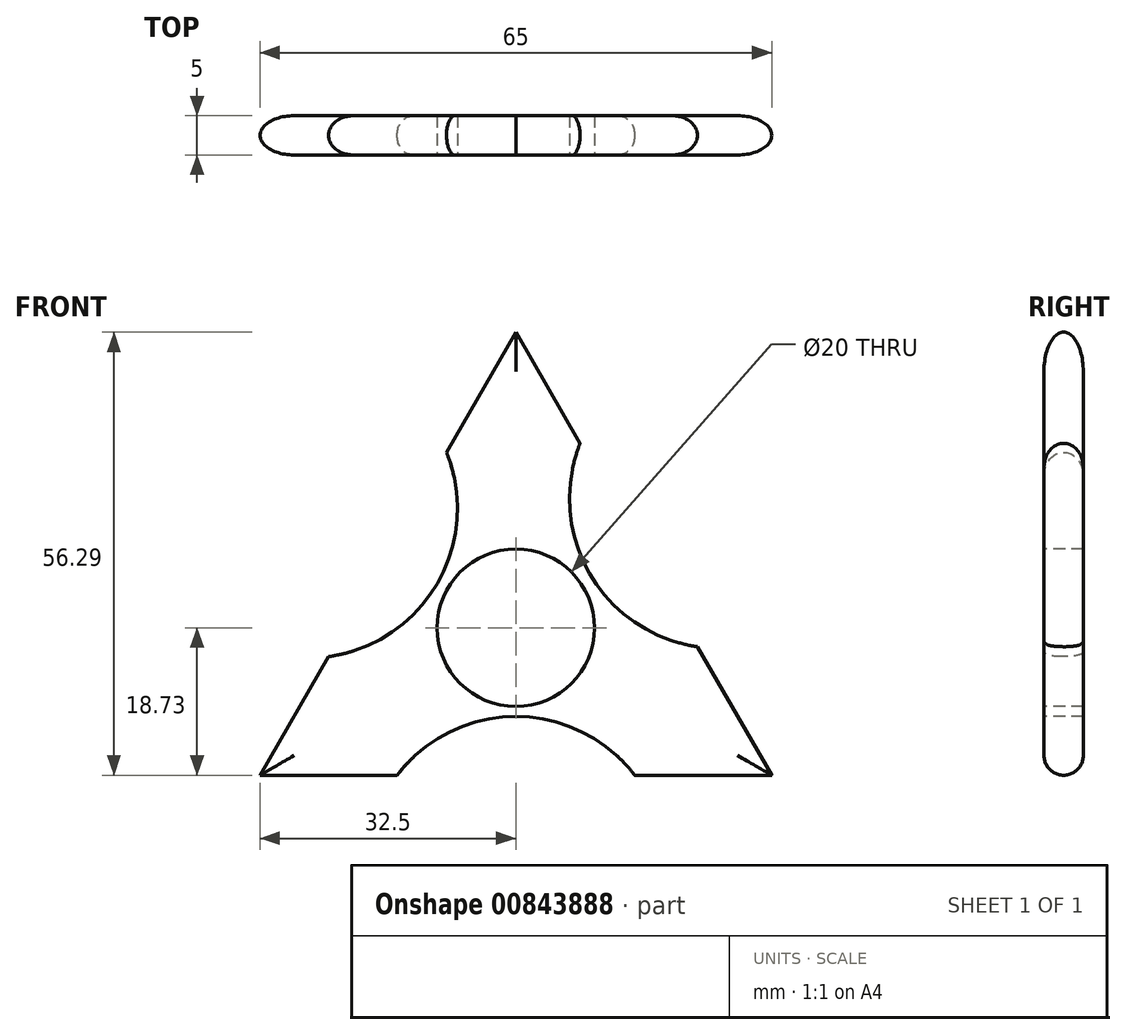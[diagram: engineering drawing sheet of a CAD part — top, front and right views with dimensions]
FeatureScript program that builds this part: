
annotation { "Feature Type Name" : "Feature", "Feature Type Description" : "" }
export const myFeature = defineFeature(function(context is Context, id is Id, definition is map)
    precondition{}
    {
        {
            var Q0;
            Q0=qCreatedBy(makeId("Front.planeOp"),FACE);
            var sketch = newSketch(context, id + "F0", { "sketchPlane" : qUnion([Q0])});
            skLineSegment(sketch, "E0", {"start": v(-32.5, 0) * mm, "end": v(32.5, 0) * mm});
            skLineSegment(sketch, "E1", {"start": v(32.5, 0) * mm, "end": v(0, 56.3) * mm});
            skLineSegment(sketch, "E2", {"start": v(0, 56.3) * mm, "end": v(-32.5, 0) * mm});
            skSolve(sketch);
        }
        {
            var Q0;
            Q0=makeQuery(id+"F0.imprint","IMPRINT",FACE,{"disambiguationData":[TD([[makeQuery(id+"F0.imprint","IMPRINT",EDGE,{"derivedFrom":sQuery(id+"F0.wireOp",EDGE,"E0")}),1.0]])]});
            var sketch = newSketch(context, id + "F1", { "sketchPlane" : qUnion([Q0])});
            skCircle(sketch, "E3", {"center": v(0, 18.73) * mm, "radius": 9.5 * mm});
            skEllipse(sketch, "E4", {"center": v(-16.73, 28.4) * mm, "majorRadius": 15 * mm, "minorRadius": 7.5 * mm, "majorAxis": v(0.52, 0.86)});
            skEllipse(sketch, "E5", {"center": v(16.42, 28.27) * mm, "majorRadius": 15 * mm, "minorRadius": 7.5 * mm, "majorAxis": v(-0.5, 0.86)});
            skEllipse(sketch, "E6", {"center": v(0, 0) * mm, "majorRadius": 15 * mm, "minorRadius": 7.5 * mm, "majorAxis": v(-1, 0)});
            skLineSegment(sketch, "E7", {"start": v(16.42, 28.27) * mm, "end": v(-32.54, 0) * mm});
            skLineSegment(sketch, "E8", {"start": v(0, 56.42) * mm, "end": v(0, 0) * mm});
            skPoint(sketch, "E9", {"position": v(32.46, 0) * mm});
            skLineSegment(sketch, "E10", {"start": v(32.46, 0) * mm, "end": v(-16.73, 28.4) * mm});
            skSolve(sketch);
        }
        {
            var Q0;
            Q0=makeQuery(id+"F0.imprint","IMPRINT",FACE,{"disambiguationData":[TD([[makeQuery(id+"F0.imprint","IMPRINT",EDGE,{"derivedFrom":sQuery(id+"F0.wireOp",EDGE,"E0")}),1.0]])]});
            extrude(context, id + "F2", {"entities" : qUnion([Q0]), "depth" : 5 * mm, "offsetDistance" : 25 * mm});
        }
        {
            var Q0;
            Q0=sQuery(id+"F1.wireOp",VERTEX,"E3.center");
            var Q1;
            Q1=makeQuery(id+"F2.opExtrude","SWEPT_BODY",BODY,{"disambiguationData":[OSD([sQuery(id+"F0.wireOp",EDGE,"E0"),sQuery(id+"F0.wireOp",EDGE,"E1"),sQuery(id+"F0.wireOp",EDGE,"E2")])]});
            hole(context, id + "F3", {"style" : HoleStyle.SIMPLE, "endStyle" : HoleEndStyle.THROUGH, "oppositeDirection" : true, "holeDiameter" : 20 * mm, "majorDiameter" : 5 * mm, "isTappedThrough" : true, "tappedDepth" : 12 * mm, "tapClearance" : 3, "startFromSketch" : true, "locations" : qUnion([Q0]), "scope" : qUnion([Q1])});
        }
        {
            var Q0;
            Q0=makeQuery(id+"F2.opExtrude","CAP_FACE",FACE,{"disambiguationData":[OSD([sQuery(id+"F0.wireOp",EDGE,"E0"),sQuery(id+"F0.wireOp",EDGE,"E1"),sQuery(id+"F0.wireOp",EDGE,"E2")])],"isStart":false});
            var sketch = newSketch(context, id + "F4", { "sketchPlane" : qUnion([Q0])});
            skArc(sketch, "E11", {"start": v(-23.8, 15.07) * mm, "mid": v(-9.97, 24.39) * mm, "end": v(-8.81, 41.02) * mm});
            skArc(sketch, "E12", {"start": v(8.16, 42.16) * mm, "mid": v(9.35, 25.63) * mm, "end": v(23.07, 16.33) * mm});
            skArc(sketch, "E13", {"start": v(15.1, 0) * mm, "mid": v(0, 7.46) * mm, "end": v(-15.1, 0) * mm});
            skSolve(sketch);
        }
        {
            var Q0;
            {var subQ0=sQuery(id+"F4.wireOp",EDGE,"E11");Q0=makeQuery(id+"F4.imprint","IMPRINT",FACE,{"disambiguationData":[TD([[makeQuery(id+"F4.imprint","IMPRINT",EDGE,{"derivedFrom":subQ0}),1.0]])]});}
            var Q1;
            {var subQ0=sQuery(id+"F4.wireOp",EDGE,"E12");Q1=makeQuery(id+"F4.imprint","IMPRINT",FACE,{"disambiguationData":[TD([[makeQuery(id+"F4.imprint","IMPRINT",EDGE,{"derivedFrom":subQ0}),1.0]])]});}
            var Q2;
            {var subQ0=sQuery(id+"F4.wireOp",EDGE,"E13");Q2=makeQuery(id+"F4.imprint","IMPRINT",FACE,{"disambiguationData":[TD([[makeQuery(id+"F4.imprint","IMPRINT",EDGE,{"derivedFrom":subQ0}),1.0]])]});}
            extrude(context, id + "F5", {"entities" : qUnion([Q0, Q1, Q2]), "operationType" : NewBodyOperationType.REMOVE, "oppositeDirection" : true, "depth" : 5 * mm, "offsetDistance" : 25 * mm});
        }
        {
            var Q0;
            {var subQ0=sQuery(id+"F0.wireOp",EDGE,"E2");var subQ1=sQuery(id+"F0.wireOp",EDGE,"E1");Q0=makeQuery(id+"F5.boolean.opBoolean","SPLIT",EDGE,{"disambiguationData":[TD([makeQuery(id+"F2.opExtrude","SWEPT_FACE",FACE,{"disambiguationData":[OSD([subQ1])]})])],"derivedFrom":makeQuery(id+"F2.opExtrude","CAP_EDGE",EDGE,{"disambiguationData":[OSD([subQ0])],"isStart":false})});}
            var Q1;
            {var subQ0=sQuery(id+"F0.wireOp",EDGE,"E2");var subQ1=sQuery(id+"F0.wireOp",EDGE,"E1");Q1=makeQuery(id+"F5.boolean.opBoolean","SPLIT",EDGE,{"disambiguationData":[TD([makeQuery(id+"F2.opExtrude","SWEPT_FACE",FACE,{"disambiguationData":[OSD([subQ0])]})])],"derivedFrom":makeQuery(id+"F2.opExtrude","CAP_EDGE",EDGE,{"disambiguationData":[OSD([subQ1])],"isStart":false})});}
            var Q2;
            {var subQ0=sQuery(id+"F0.wireOp",EDGE,"E0");var subQ1=sQuery(id+"F0.wireOp",EDGE,"E1");Q2=makeQuery(id+"F5.boolean.opBoolean","SPLIT",EDGE,{"disambiguationData":[TD([makeQuery(id+"F2.opExtrude","SWEPT_FACE",FACE,{"disambiguationData":[OSD([subQ0])]})])],"derivedFrom":makeQuery(id+"F2.opExtrude","CAP_EDGE",EDGE,{"disambiguationData":[OSD([subQ1])],"isStart":false})});}
            var Q3;
            {var subQ0=sQuery(id+"F0.wireOp",EDGE,"E0");var subQ1=sQuery(id+"F0.wireOp",EDGE,"E1");Q3=makeQuery(id+"F5.boolean.opBoolean","SPLIT",EDGE,{"disambiguationData":[TD([makeQuery(id+"F2.opExtrude","SWEPT_FACE",FACE,{"disambiguationData":[OSD([subQ1])]})])],"derivedFrom":makeQuery(id+"F2.opExtrude","CAP_EDGE",EDGE,{"disambiguationData":[OSD([subQ0])],"isStart":false})});}
            var Q4;
            {var subQ0=sQuery(id+"F0.wireOp",EDGE,"E0");var subQ1=sQuery(id+"F0.wireOp",EDGE,"E2");Q4=makeQuery(id+"F5.boolean.opBoolean","SPLIT",EDGE,{"disambiguationData":[TD([makeQuery(id+"F2.opExtrude","SWEPT_FACE",FACE,{"disambiguationData":[OSD([subQ1])]})])],"derivedFrom":makeQuery(id+"F2.opExtrude","CAP_EDGE",EDGE,{"disambiguationData":[OSD([subQ0])],"isStart":false})});}
            var Q5;
            {var subQ0=sQuery(id+"F0.wireOp",EDGE,"E0");var subQ1=sQuery(id+"F0.wireOp",EDGE,"E2");Q5=makeQuery(id+"F5.boolean.opBoolean","SPLIT",EDGE,{"disambiguationData":[TD([makeQuery(id+"F2.opExtrude","SWEPT_FACE",FACE,{"disambiguationData":[OSD([subQ0])]})])],"derivedFrom":makeQuery(id+"F2.opExtrude","CAP_EDGE",EDGE,{"disambiguationData":[OSD([subQ1])],"isStart":false})});}
            var Q6;
            Q6=makeQuery(id+"F5.boolean.opBoolean","COPY",EDGE,{"derivedFrom":makeQuery(id+"F5.opExtrude","CAP_EDGE",EDGE,{"disambiguationData":[OSD([sQuery(id+"F4.wireOp",EDGE,"E11")])],"isStart":true})});
            var Q7;
            Q7=makeQuery(id+"F5.boolean.opBoolean","COPY",EDGE,{"derivedFrom":makeQuery(id+"F5.opExtrude","CAP_EDGE",EDGE,{"disambiguationData":[OSD([sQuery(id+"F4.wireOp",EDGE,"E12")])],"isStart":true})});
            var Q8;
            Q8=makeQuery(id+"F5.boolean.opBoolean","COPY",EDGE,{"derivedFrom":makeQuery(id+"F5.opExtrude","CAP_EDGE",EDGE,{"disambiguationData":[OSD([sQuery(id+"F4.wireOp",EDGE,"E13")])],"isStart":true})});
            fillet(context, id + "F6", {"entities" : qUnion([Q0, Q1, Q2, Q3, Q4, Q5, Q6, Q7, Q8]), "radius" : 2.5 * mm, "tangentPropagation" : true, "allowEdgeOverflow" : false});
        }
        {
            var Q0;
            {var subQ0=sQuery(id+"F0.wireOp",EDGE,"E2");var subQ1=sQuery(id+"F0.wireOp",EDGE,"E1");Q0=makeQuery(id+"F5.boolean.opBoolean","SPLIT",EDGE,{"disambiguationData":[TD([makeQuery(id+"F2.opExtrude","SWEPT_FACE",FACE,{"disambiguationData":[OSD([subQ0])]})])],"derivedFrom":makeQuery(id+"F2.opExtrude","CAP_EDGE",EDGE,{"disambiguationData":[OSD([subQ1])],"isStart":true})});}
            var Q1;
            {var subQ0=sQuery(id+"F0.wireOp",EDGE,"E2");var subQ1=sQuery(id+"F0.wireOp",EDGE,"E1");Q1=makeQuery(id+"F5.boolean.opBoolean","SPLIT",EDGE,{"disambiguationData":[TD([makeQuery(id+"F2.opExtrude","SWEPT_FACE",FACE,{"disambiguationData":[OSD([subQ1])]})])],"derivedFrom":makeQuery(id+"F2.opExtrude","CAP_EDGE",EDGE,{"disambiguationData":[OSD([subQ0])],"isStart":true})});}
            var Q2;
            Q2=makeQuery(id+"F5.boolean.opBoolean","COPY",EDGE,{"derivedFrom":makeQuery(id+"F5.opExtrude","CAP_EDGE",EDGE,{"disambiguationData":[OSD([sQuery(id+"F4.wireOp",EDGE,"E12")])],"isStart":false})});
            var Q3;
            {var subQ0=sQuery(id+"F0.wireOp",EDGE,"E0");var subQ1=sQuery(id+"F0.wireOp",EDGE,"E1");Q3=makeQuery(id+"F5.boolean.opBoolean","SPLIT",EDGE,{"disambiguationData":[TD([makeQuery(id+"F2.opExtrude","SWEPT_FACE",FACE,{"disambiguationData":[OSD([subQ0])]})])],"derivedFrom":makeQuery(id+"F2.opExtrude","CAP_EDGE",EDGE,{"disambiguationData":[OSD([subQ1])],"isStart":true})});}
            var Q4;
            {var subQ0=sQuery(id+"F0.wireOp",EDGE,"E0");var subQ1=sQuery(id+"F0.wireOp",EDGE,"E1");Q4=makeQuery(id+"F5.boolean.opBoolean","SPLIT",EDGE,{"disambiguationData":[TD([makeQuery(id+"F2.opExtrude","SWEPT_FACE",FACE,{"disambiguationData":[OSD([subQ1])]})])],"derivedFrom":makeQuery(id+"F2.opExtrude","CAP_EDGE",EDGE,{"disambiguationData":[OSD([subQ0])],"isStart":true})});}
            var Q5;
            Q5=makeQuery(id+"F5.boolean.opBoolean","COPY",EDGE,{"derivedFrom":makeQuery(id+"F5.opExtrude","CAP_EDGE",EDGE,{"disambiguationData":[OSD([sQuery(id+"F4.wireOp",EDGE,"E13")])],"isStart":false})});
            var Q6;
            {var subQ0=sQuery(id+"F0.wireOp",EDGE,"E0");var subQ1=sQuery(id+"F0.wireOp",EDGE,"E2");Q6=makeQuery(id+"F5.boolean.opBoolean","SPLIT",EDGE,{"disambiguationData":[TD([makeQuery(id+"F2.opExtrude","SWEPT_FACE",FACE,{"disambiguationData":[OSD([subQ1])]})])],"derivedFrom":makeQuery(id+"F2.opExtrude","CAP_EDGE",EDGE,{"disambiguationData":[OSD([subQ0])],"isStart":true})});}
            var Q7;
            {var subQ0=sQuery(id+"F0.wireOp",EDGE,"E0");var subQ1=sQuery(id+"F0.wireOp",EDGE,"E2");Q7=makeQuery(id+"F5.boolean.opBoolean","SPLIT",EDGE,{"disambiguationData":[TD([makeQuery(id+"F2.opExtrude","SWEPT_FACE",FACE,{"disambiguationData":[OSD([subQ0])]})])],"derivedFrom":makeQuery(id+"F2.opExtrude","CAP_EDGE",EDGE,{"disambiguationData":[OSD([subQ1])],"isStart":true})});}
            var Q8;
            Q8=makeQuery(id+"F5.boolean.opBoolean","COPY",EDGE,{"derivedFrom":makeQuery(id+"F5.opExtrude","CAP_EDGE",EDGE,{"disambiguationData":[OSD([sQuery(id+"F4.wireOp",EDGE,"E11")])],"isStart":false})});
            fillet(context, id + "F7", {"entities" : qUnion([Q0, Q1, Q2, Q3, Q4, Q5, Q6, Q7, Q8]), "radius" : 2.5 * mm, "tangentPropagation" : true, "allowEdgeOverflow" : false});
        }
    });
